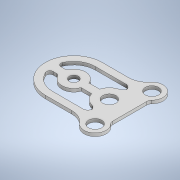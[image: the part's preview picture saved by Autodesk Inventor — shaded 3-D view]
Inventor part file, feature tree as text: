
AUTODESK INVENTOR PART (.ipt)
format: ipt  version: 2021 (Build 250183000, 183)  size: 203,776 bytes
history: native  units: mm
features: extrude x1, sketch x1
ambient origin geometry x8: Origin, YZ Plane, XZ Plane, XY Plane, X Axis, Y Axis, Z Axis, Center Point
bodies: Solid1 (feature_tree)
feature tree (2):
  extrude  "Extrusion1"  Depth=10.0mm
  sketch  "Sketch1"  dims[d0=180.0mm d1=20.0mm d2=20.0mm d3=42.0mm d4=70.0mm d5=42.0mm d6=70.0mm d7=112.5mm d8=90.0mm d9=90.0mm d10=25.0mm d11=90.0mm d12=68.0mm d13=77.5mm d14=37.5mm d15=37.5mm d16=29.0mm d17=45.0mm d18=45.0mm d19=42.0mm d20=25.0mm d21=77.5mm d22=112.5mm d23=112.5mm d24=45.0mm d25=68.0mm d26=2.0mm d27=10.0mm d28=15.0mm d29=60.0mm d30=10.0mm d31=0.0mm]
